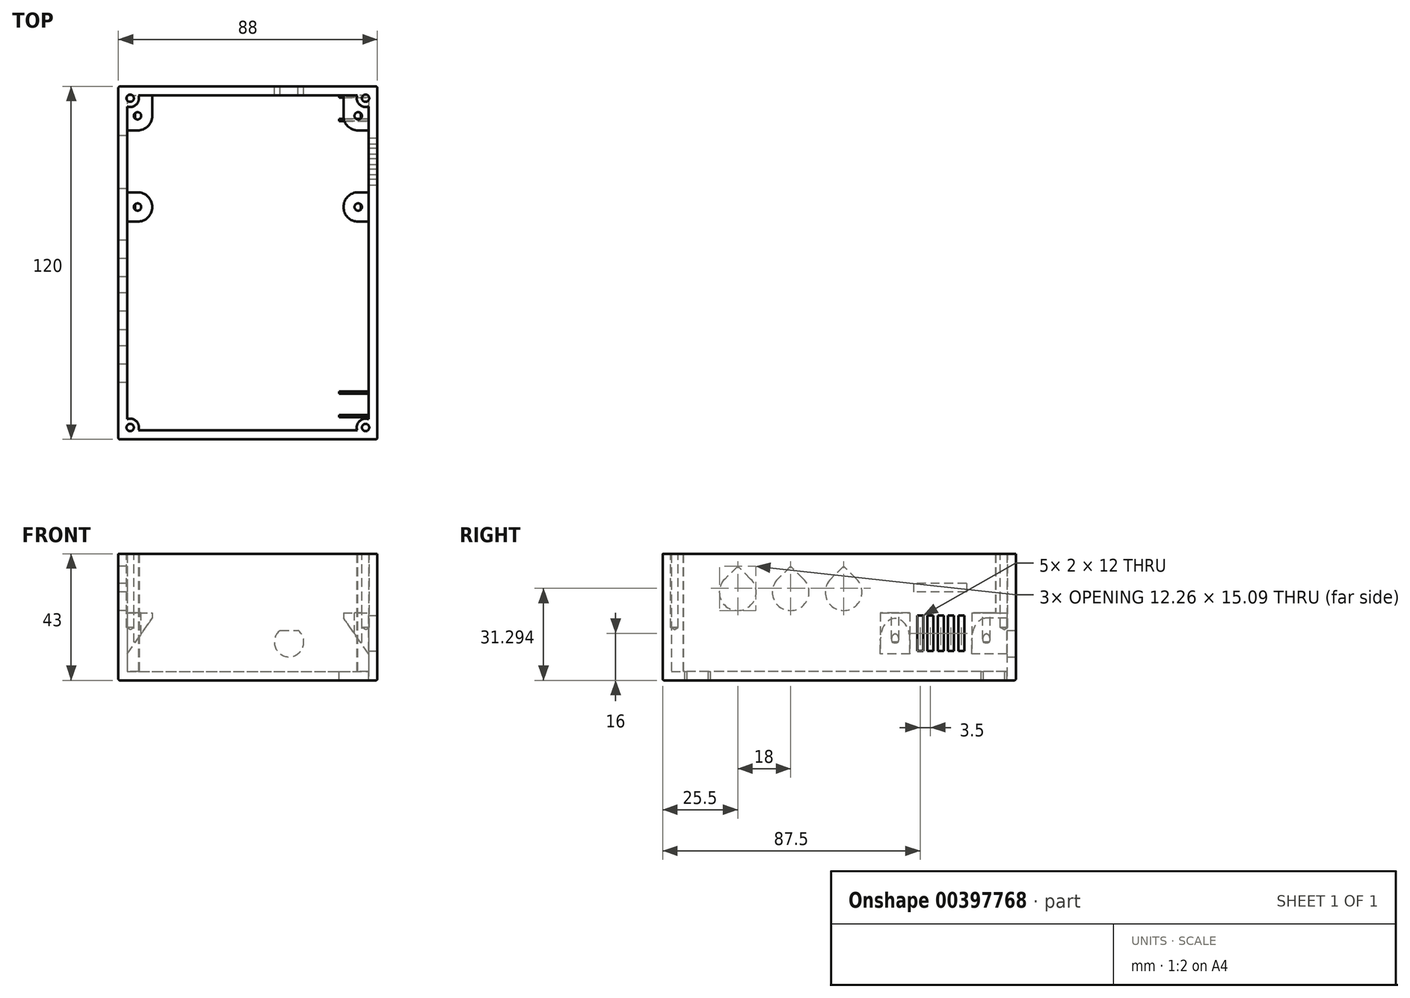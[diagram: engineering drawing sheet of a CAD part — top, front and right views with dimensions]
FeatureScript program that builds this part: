
annotation { "Feature Type Name" : "Feature", "Feature Type Description" : "" }
export const myFeature = defineFeature(function(context is Context, id is Id, definition is map)
    precondition{}
    {
        {
            var Q0;
            Q0=qCreatedBy(makeId("Top.planeOp"),FACE);
            var sketch = newSketch(context, id + "F0", { "sketchPlane" : qUnion([Q0])});
            skLineSegment(sketch, "E0.bottom", {"start": v(0, 0) * mm, "end": v(88, 0) * mm});
            skLineSegment(sketch, "E0.top", {"start": v(0, 120) * mm, "end": v(88, 120) * mm});
            skLineSegment(sketch, "E0.left", {"start": v(0, 0) * mm, "end": v(0, 120) * mm});
            skLineSegment(sketch, "E0.right", {"start": v(88, 0) * mm, "end": v(88, 120) * mm});
            skSolve(sketch);
        }
        {
            var Q0;
            Q0 = qSketchRegion(id + "F0", true);
            extrude(context, id + "F1", {"entities" : qUnion([Q0]), "depth" : 3 * mm});
        }
        {
            var Q0;
            Q0=makeQuery(id+"F1.opExtrude","CAP_FACE",FACE,{"disambiguationData":[OSD([sQuery(id+"F0.wireOp",EDGE,"E0.bottom"),sQuery(id+"F0.wireOp",EDGE,"E0.top"),sQuery(id+"F0.wireOp",EDGE,"E0.left"),sQuery(id+"F0.wireOp",EDGE,"E0.right")])],"isStart":false});
            var sketch = newSketch(context, id + "F2", { "sketchPlane" : qUnion([Q0])});
            skLineSegment(sketch, "E1.0", {"start": v(0, 0) * mm, "end": v(0, 120) * mm});
            skLineSegment(sketch, "E2.0", {"start": v(0, 120) * mm, "end": v(88, 120) * mm});
            skLineSegment(sketch, "E3.0", {"start": v(88, 0) * mm, "end": v(88, 120) * mm});
            skLineSegment(sketch, "E4.0", {"start": v(0, 0) * mm, "end": v(88, 0) * mm});
            skLineSegment(sketch, "E5.bottom", {"start": v(6.83, 117) * mm, "end": v(81.17, 117) * mm});
            skLineSegment(sketch, "E5.top", {"start": v(6.83, 3) * mm, "end": v(81.17, 3) * mm});
            skLineSegment(sketch, "E5.left", {"start": v(3, 113.17) * mm, "end": v(3, 6.83) * mm});
            skLineSegment(sketch, "E5.right", {"start": v(85, 113.17) * mm, "end": v(85, 6.83) * mm});
            skArc(sketch, "E6", {"start": v(3, 113.17) * mm, "mid": v(6.12, 113.88) * mm, "end": v(6.83, 117) * mm});
            skArc(sketch, "E7", {"start": v(81.17, 117) * mm, "mid": v(81.88, 113.88) * mm, "end": v(85, 113.17) * mm});
            skArc(sketch, "E8", {"start": v(6.83, 3) * mm, "mid": v(6.12, 6.12) * mm, "end": v(3, 6.83) * mm});
            skArc(sketch, "E9", {"start": v(85, 6.83) * mm, "mid": v(81.88, 6.12) * mm, "end": v(81.17, 3) * mm});
            skSolve(sketch);
        }
        {
            var Q0;
            Q0 = qSketchRegion(id + "F2", true);
            extrude(context, id + "F3", {"entities" : qUnion([Q0]), "operationType" : NewBodyOperationType.ADD, "depth" : 40 * mm});
        }
        {
            var Q0;
            Q0=makeQuery(id+"F3.boolean.opBoolean","MERGE",FACE,{"derivedFrom":[makeQuery(id+"F1.opExtrude","SWEPT_FACE",FACE,{"disambiguationData":[OSD([sQuery(id+"F0.wireOp",EDGE,"E0.left")])]}),makeQuery(id+"F3.opExtrude","SWEPT_FACE",FACE,{"disambiguationData":[OSD([sQuery(id+"F2.wireOp",EDGE,"E1.0")])]})]});
            var sketch = newSketch(context, id + "F4", { "sketchPlane" : qUnion([Q0])});
            skArc(sketch, "E10", {"start": v(-65.92, 34.42) * mm, "mid": v(-61.5, 23.75) * mm, "end": v(-57.08, 34.42) * mm});
            skLineSegment(sketch, "E11", {"start": v(-65.92, 34.42) * mm, "end": v(-61.5, 38.84) * mm});
            skLineSegment(sketch, "E12", {"start": v(-61.5, 38.84) * mm, "end": v(-57.08, 34.42) * mm});
            skLineSegment(sketch, "E13.1.0.0", {"start": v(-43.5, 38.84) * mm, "end": v(-39.08, 34.42) * mm});
            skLineSegment(sketch, "E13.1.0.1", {"start": v(-47.92, 34.42) * mm, "end": v(-43.5, 38.84) * mm});
            skArc(sketch, "E13.1.0.2", {"start": v(-47.92, 34.42) * mm, "mid": v(-43.5, 23.75) * mm, "end": v(-39.08, 34.42) * mm});
            skLineSegment(sketch, "E13.2.0.0", {"start": v(-25.5, 38.84) * mm, "end": v(-21.08, 34.42) * mm});
            skLineSegment(sketch, "E13.2.0.1", {"start": v(-29.92, 34.42) * mm, "end": v(-25.5, 38.84) * mm});
            skArc(sketch, "E13.2.0.2", {"start": v(-29.92, 34.42) * mm, "mid": v(-25.5, 23.75) * mm, "end": v(-21.08, 34.42) * mm});
            skLineSegment(sketch, "E13.direction1", {"start": v(-61.5, 30) * mm, "end": v(-43.5, 30) * mm, "construction": true});
            skSolve(sketch);
        }
        {
            var Q0;
            Q0 = qSketchRegion(id + "F4", true);
            extrude(context, id + "F5", {"entities" : qUnion([Q0]), "operationType" : NewBodyOperationType.REMOVE, "endBound" : BoundingType.UP_TO_NEXT, "oppositeDirection" : true, "depth" : 25 * mm});
        }
        {
            var Q0;
            Q0=makeQuery(id+"F3.boolean.opBoolean","MERGE",FACE,{"derivedFrom":[makeQuery(id+"F1.opExtrude","SWEPT_FACE",FACE,{"disambiguationData":[OSD([sQuery(id+"F0.wireOp",EDGE,"E0.top")])]}),makeQuery(id+"F3.opExtrude","SWEPT_FACE",FACE,{"disambiguationData":[OSD([sQuery(id+"F2.wireOp",EDGE,"E2.0")])]})]});
            var sketch = newSketch(context, id + "F6", { "sketchPlane" : qUnion([Q0])});
            skArc(sketch, "E14", {"start": v(-61.07, 16.95) * mm, "mid": v(-58, 8) * mm, "end": v(-54.93, 16.95) * mm});
            skLineSegment(sketch, "E15", {"start": v(-61.07, 16.95) * mm, "end": v(-54.93, 16.95) * mm});
            skSolve(sketch);
        }
        {
            var Q0;
            Q0 = qSketchRegion(id + "F6", true);
            extrude(context, id + "F7", {"entities" : qUnion([Q0]), "operationType" : NewBodyOperationType.REMOVE, "endBound" : BoundingType.UP_TO_NEXT, "oppositeDirection" : true, "depth" : 25 * mm});
        }
        {
            var Q0;
            Q0=makeQuery(id+"F1.opExtrude","CAP_EDGE",EDGE,{"disambiguationData":[OSD([sQuery(id+"F0.wireOp",EDGE,"E0.left")])],"isStart":true});
            var Q1;
            Q1=makeQuery(id+"F1.opExtrude","CAP_EDGE",EDGE,{"disambiguationData":[OSD([sQuery(id+"F0.wireOp",EDGE,"E0.bottom")])],"isStart":true});
            var Q2;
            Q2=makeQuery(id+"F3.boolean.opBoolean","MERGE",EDGE,{"derivedFrom":[makeQuery(id+"F1.opExtrude","SWEPT_EDGE",EDGE,{"disambiguationData":[OSD([sQuery(id+"F0.wireOp",EDGE,"E0.bottom"),sQuery(id+"F0.wireOp",EDGE,"E0.left")])]}),makeQuery(id+"F3.opExtrude","SWEPT_EDGE",EDGE,{"disambiguationData":[OSD([sQuery(id+"F2.wireOp",EDGE,"E1.0"),sQuery(id+"F2.wireOp",EDGE,"E4.0")])]})]});
            var Q3;
            Q3=makeQuery(id+"F3.boolean.opBoolean","MERGE",EDGE,{"derivedFrom":[makeQuery(id+"F1.opExtrude","SWEPT_EDGE",EDGE,{"disambiguationData":[OSD([sQuery(id+"F0.wireOp",EDGE,"E0.top"),sQuery(id+"F0.wireOp",EDGE,"E0.left")])]}),makeQuery(id+"F3.opExtrude","SWEPT_EDGE",EDGE,{"disambiguationData":[OSD([sQuery(id+"F2.wireOp",EDGE,"E1.0"),sQuery(id+"F2.wireOp",EDGE,"E2.0")])]})]});
            var Q4;
            Q4=makeQuery(id+"F3.boolean.opBoolean","MERGE",EDGE,{"derivedFrom":[makeQuery(id+"F1.opExtrude","SWEPT_EDGE",EDGE,{"disambiguationData":[OSD([sQuery(id+"F0.wireOp",EDGE,"E0.bottom"),sQuery(id+"F0.wireOp",EDGE,"E0.right")])]}),makeQuery(id+"F3.opExtrude","SWEPT_EDGE",EDGE,{"disambiguationData":[OSD([sQuery(id+"F2.wireOp",EDGE,"E3.0"),sQuery(id+"F2.wireOp",EDGE,"E4.0")])]})]});
            var Q5;
            Q5=makeQuery(id+"F1.opExtrude","CAP_EDGE",EDGE,{"disambiguationData":[OSD([sQuery(id+"F0.wireOp",EDGE,"E0.right")])],"isStart":true});
            var Q6;
            Q6=makeQuery(id+"F1.opExtrude","CAP_EDGE",EDGE,{"disambiguationData":[OSD([sQuery(id+"F0.wireOp",EDGE,"E0.top")])],"isStart":true});
            var Q7;
            Q7=makeQuery(id+"F3.boolean.opBoolean","MERGE",EDGE,{"derivedFrom":[makeQuery(id+"F1.opExtrude","SWEPT_EDGE",EDGE,{"disambiguationData":[OSD([sQuery(id+"F0.wireOp",EDGE,"E0.top"),sQuery(id+"F0.wireOp",EDGE,"E0.right")])]}),makeQuery(id+"F3.opExtrude","SWEPT_EDGE",EDGE,{"disambiguationData":[OSD([sQuery(id+"F2.wireOp",EDGE,"E2.0"),sQuery(id+"F2.wireOp",EDGE,"E3.0")])]})]});
            fillet(context, id + "F8", {"entities" : qUnion([Q0, Q1, Q2, Q3, Q4, Q5, Q6, Q7]), "radius" : 0.5 * mm, "tangentPropagation" : true, "allowEdgeOverflow" : false});
        }
        {
            var Q0;
            Q0=makeQuery(id+"F1.opExtrude","CAP_FACE",FACE,{"disambiguationData":[OSD([sQuery(id+"F0.wireOp",EDGE,"E0.bottom"),sQuery(id+"F0.wireOp",EDGE,"E0.top"),sQuery(id+"F0.wireOp",EDGE,"E0.left"),sQuery(id+"F0.wireOp",EDGE,"E0.right")])],"isStart":false});
            var sketch = newSketch(context, id + "F9", { "sketchPlane" : qUnion([Q0])});
            skLineSegment(sketch, "E16.bottom", {"start": v(6.5, 110) * mm, "end": v(81.5, 110) * mm, "construction": true});
            skLineSegment(sketch, "E16.top", {"start": v(6.5, 79) * mm, "end": v(81.5, 79) * mm, "construction": true});
            skLineSegment(sketch, "E16.left", {"start": v(6.5, 110) * mm, "end": v(6.5, 79) * mm, "construction": true});
            skLineSegment(sketch, "E16.right", {"start": v(81.5, 110) * mm, "end": v(81.5, 79) * mm, "construction": true});
            skArc(sketch, "E17", {"start": v(6.5, 105) * mm, "mid": v(10.04, 106.46) * mm, "end": v(11.5, 110) * mm});
            skArc(sketch, "E18", {"start": v(76.5, 110) * mm, "mid": v(77.96, 106.46) * mm, "end": v(81.5, 105) * mm});
            skArc(sketch, "E19", {"start": v(6.5, 74) * mm, "mid": v(11.5, 79) * mm, "end": v(6.5, 84) * mm});
            skArc(sketch, "E20", {"start": v(81.5, 84) * mm, "mid": v(76.5, 79) * mm, "end": v(81.5, 74) * mm});
            skPoint(sketch, "E21", {"position": v(44, 110) * mm});
            skLineSegment(sketch, "E22", {"start": v(11.5, 110) * mm, "end": v(11.5, 117) * mm});
            skLineSegment(sketch, "E23", {"start": v(6.5, 105) * mm, "end": v(3, 105) * mm});
            skLineSegment(sketch, "E24", {"start": v(6.5, 84) * mm, "end": v(3, 84) * mm});
            skLineSegment(sketch, "E25", {"start": v(6.5, 74) * mm, "end": v(3, 74) * mm});
            skLineSegment(sketch, "E26", {"start": v(81.5, 84) * mm, "end": v(85, 84) * mm});
            skLineSegment(sketch, "E27", {"start": v(76.5, 110) * mm, "end": v(76.5, 117) * mm});
            skLineSegment(sketch, "E28", {"start": v(81.5, 105) * mm, "end": v(85, 105) * mm});
            skLineSegment(sketch, "E29", {"start": v(81.5, 74) * mm, "end": v(85, 74) * mm});
            skSolve(sketch);
        }
        {
            var Q0;
            Q0=makeQuery(id+"F9.imprint","IMPRINT",FACE,{"disambiguationData":[TD([[makeQuery(id+"F9.imprint","IMPRINT",EDGE,{"derivedFrom":sQuery(id+"F9.wireOp",EDGE,"E19")}),1.0]])]});
            var Q1;
            Q1=makeQuery(id+"F9.imprint","IMPRINT",FACE,{"disambiguationData":[TD([[makeQuery(id+"F9.imprint","IMPRINT",EDGE,{"derivedFrom":sQuery(id+"F9.wireOp",EDGE,"E17")}),1.0]])]});
            var Q2;
            Q2=makeQuery(id+"F9.imprint","IMPRINT",FACE,{"disambiguationData":[TD([[makeQuery(id+"F9.imprint","IMPRINT",EDGE,{"derivedFrom":sQuery(id+"F9.wireOp",EDGE,"E18")}),1.0]])]});
            var Q3;
            Q3=makeQuery(id+"F9.imprint","IMPRINT",FACE,{"disambiguationData":[TD([[makeQuery(id+"F9.imprint","IMPRINT",EDGE,{"derivedFrom":sQuery(id+"F9.wireOp",EDGE,"E20")}),1.0]])]});
            var Q4;
            Q4 = qBodyType(qCreatedBy(id + "F11" ,FACE), BodyType.SOLID);
            extrude(context, id + "F10", {"entities" : qUnion([Q0, Q1, Q2, Q3]), "operationType" : NewBodyOperationType.ADD, "endBoundEntityFace" : qUnion([Q4]), "depth" : 20 * mm});
        }
        {
            var Q0;
            Q0=makeQuery(id+"F3.opExtrude","CAP_FACE",FACE,{"disambiguationData":[OSD([sQuery(id+"F2.wireOp",EDGE,"E1.0"),sQuery(id+"F2.wireOp",EDGE,"E2.0"),sQuery(id+"F2.wireOp",EDGE,"E3.0"),sQuery(id+"F2.wireOp",EDGE,"E4.0"),sQuery(id+"F2.wireOp",EDGE,"E5.bottom"),sQuery(id+"F2.wireOp",EDGE,"E5.top"),sQuery(id+"F2.wireOp",EDGE,"E5.left"),sQuery(id+"F2.wireOp",EDGE,"E5.right"),sQuery(id+"F2.wireOp",EDGE,"RnDwJznH-ddYd-c09x-nSyI-hqBMwT2M9eLy"),sQuery(id+"F2.wireOp",EDGE,"lanDXxh8-xAsg-iwlZ-IwJ3-5rcP5cadt3KI"),sQuery(id+"F2.wireOp",EDGE,"uzteUbjJ-Ywx2-gnPR-lJzB-qWgk53przGQ1"),sQuery(id+"F2.wireOp",EDGE,"n90Oo4IX-6F6r-3Tcr-m6S5-17WScgTX6qWq")])],"isStart":false});
            cPlane(context, id + "F11", {"entities" : qUnion([Q0]), "cplaneType" : CPlaneType.OFFSET, "offset" : 20 * mm, "oppositeDirection" : true, "width" : 150 * mm, "height" : 150 * mm});
        }
        {
            var Q0;
            Q0=qCreatedBy(id+"F11.planeOp",FACE);
            var sketch = newSketch(context, id + "F12", { "sketchPlane" : qUnion([Q0])});
            skArc(sketch, "E30.0", {"start": v(6.5, 105) * mm, "mid": v(10.04, 106.46) * mm, "end": v(11.5, 110) * mm, "construction": true});
            skArc(sketch, "E31.0", {"start": v(6.5, 74) * mm, "mid": v(11.5, 79) * mm, "end": v(6.5, 84) * mm, "construction": true});
            skArc(sketch, "E32.0", {"start": v(81.5, 84) * mm, "mid": v(76.5, 79) * mm, "end": v(81.5, 74) * mm, "construction": true});
            skArc(sketch, "E33.0", {"start": v(76.5, 110) * mm, "mid": v(77.96, 106.46) * mm, "end": v(81.5, 105) * mm, "construction": true});
            skSolve(sketch);
        }
        {
            var Q0;
            Q0=sQuery(id+"F12.wireOp",VERTEX,"E30.0.center");
            var Q1;
            Q1=sQuery(id+"F12.wireOp",VERTEX,"E31.0.center");
            var Q2;
            Q2=sQuery(id+"F12.wireOp",VERTEX,"E32.0.center");
            var Q3;
            Q3=sQuery(id+"F12.wireOp",VERTEX,"E33.0.center");
            var Q4;
            Q4=makeQuery(id+"F1.opExtrude","SWEPT_BODY",BODY,{"disambiguationData":[OSD([sQuery(id+"F0.wireOp",EDGE,"E0.bottom"),sQuery(id+"F0.wireOp",EDGE,"E0.top"),sQuery(id+"F0.wireOp",EDGE,"E0.left"),sQuery(id+"F0.wireOp",EDGE,"E0.right")])]});
            hole(context, id + "F13", {"style" : HoleStyle.SIMPLE, "endStyle" : HoleEndStyle.BLIND, "holeDiameter" : 2.5 * mm, "holeDepth" : 10 * mm, "isTappedThrough" : true, "tappedDepth" : 12 * mm, "tapClearance" : 3, "locations" : qUnion([Q0, Q1, Q2, Q3]), "scope" : qUnion([Q4])});
        }
        {
            var Q0;
            Q0=makeQuery(id+"F10.opExtrude","SWEPT_FACE",FACE,{"disambiguationData":[OSD([sQuery(id+"F9.wireOp",EDGE,"E29")])]});
            var sketch = newSketch(context, id + "F14", { "sketchPlane" : qUnion([Q0])});
            skLineSegment(sketch, "E34", {"start": v(85, 3) * mm, "end": v(85, 9) * mm});
            skLineSegment(sketch, "E35", {"start": v(85, 9) * mm, "end": v(76.5, 21.14) * mm});
            skLineSegment(sketch, "E36", {"start": v(76.5, 21.14) * mm, "end": v(76.5, 3) * mm});
            skLineSegment(sketch, "E37", {"start": v(76.5, 3) * mm, "end": v(85, 3) * mm});
            skSolve(sketch);
        }
        {
            var Q0;
            Q0 = qSketchRegion(id + "F14", true);
            var Q1;
            Q1=makeQuery(id+"F3.opExtrude","SWEPT_FACE",FACE,{"disambiguationData":[OSD([sQuery(id+"F2.wireOp",EDGE,"E5.bottom")])]});
            extrude(context, id + "F15", {"entities" : qUnion([Q0]), "operationType" : NewBodyOperationType.REMOVE, "endBound" : BoundingType.UP_TO_SURFACE, "oppositeDirection" : true, "endBoundEntityFace" : qUnion([Q1]), "depth" : 25 * mm});
        }
        {
            var Q0;
            Q0=makeQuery(id+"F10.opExtrude","SWEPT_FACE",FACE,{"disambiguationData":[OSD([sQuery(id+"F9.wireOp",EDGE,"E25")])]});
            var sketch = newSketch(context, id + "F16", { "sketchPlane" : qUnion([Q0])});
            skLineSegment(sketch, "E38", {"start": v(3, 3) * mm, "end": v(3, 9) * mm});
            skLineSegment(sketch, "E39", {"start": v(3, 9) * mm, "end": v(11.5, 21.14) * mm});
            skLineSegment(sketch, "E40", {"start": v(11.5, 21.14) * mm, "end": v(11.5, 3) * mm});
            skLineSegment(sketch, "E41", {"start": v(11.5, 3) * mm, "end": v(3, 3) * mm});
            skSolve(sketch);
        }
        {
            var Q0;
            Q0 = qSketchRegion(id + "F16", true);
            var Q1;
            {var subQ0=sQuery(id+"F2.wireOp",EDGE,"E5.bottom");Q1=makeQuery(id+"F15.boolean.opBoolean","MERGE",FACE,{"derivedFrom":[makeQuery(id+"F3.opExtrude","SWEPT_FACE",FACE,{"disambiguationData":[OSD([subQ0])]}),makeQuery(id+"F15.opExtrude","CAP_FACE",FACE,{"disambiguationData":[OSD([subQ0])],"isStart":false})]});}
            extrude(context, id + "F17", {"entities" : qUnion([Q0]), "operationType" : NewBodyOperationType.REMOVE, "endBound" : BoundingType.UP_TO_SURFACE, "oppositeDirection" : true, "endBoundEntityFace" : qUnion([Q1]), "depth" : 25 * mm});
        }
        {
            var Q0;
            Q0=makeQuery(id+"F17.boolean.opBoolean","MERGE",FACE,{"derivedFrom":[makeQuery(id+"F15.boolean.opBoolean","MERGE",FACE,{"derivedFrom":[makeQuery(id+"F1.opExtrude","CAP_FACE",FACE,{"disambiguationData":[OSD([sQuery(id+"F0.wireOp",EDGE,"E0.bottom"),sQuery(id+"F0.wireOp",EDGE,"E0.top"),sQuery(id+"F0.wireOp",EDGE,"E0.left"),sQuery(id+"F0.wireOp",EDGE,"E0.right")])],"isStart":false}),makeQuery(id+"F15.opExtrude","SWEPT_FACE",FACE,{"disambiguationData":[OSD([sQuery(id+"F14.wireOp",EDGE,"E37")])]})]}),makeQuery(id+"F17.opExtrude","SWEPT_FACE",FACE,{"disambiguationData":[OSD([sQuery(id+"F16.wireOp",EDGE,"E41")])]})]});
            var sketch = newSketch(context, id + "F18", { "sketchPlane" : qUnion([Q0])});
            skLineSegment(sketch, "E42.bottom", {"start": v(75, 8.25) * mm, "end": v(85, 8.25) * mm});
            skLineSegment(sketch, "E42.top", {"start": v(75, 7.5) * mm, "end": v(85, 7.5) * mm});
            skLineSegment(sketch, "E42.left", {"start": v(75, 7.5) * mm, "end": v(75, 8.25) * mm});
            skLineSegment(sketch, "E42.right", {"start": v(85, 7.5) * mm, "end": v(85, 8.25) * mm});
            skLineSegment(sketch, "E43.bottom", {"start": v(75, 15.5) * mm, "end": v(85, 15.5) * mm});
            skLineSegment(sketch, "E43.top", {"start": v(75, 16.25) * mm, "end": v(85, 16.25) * mm});
            skLineSegment(sketch, "E43.left", {"start": v(75, 15.5) * mm, "end": v(75, 16.25) * mm});
            skLineSegment(sketch, "E43.right", {"start": v(85, 15.5) * mm, "end": v(85, 16.25) * mm});
            skLineSegment(sketch, "E44.bottom", {"start": v(75, 108.25) * mm, "end": v(85, 108.25) * mm});
            skLineSegment(sketch, "E44.top", {"start": v(75, 109) * mm, "end": v(85, 109) * mm});
            skLineSegment(sketch, "E44.left", {"start": v(75, 108.25) * mm, "end": v(75, 109) * mm});
            skLineSegment(sketch, "E44.right", {"start": v(85, 108.25) * mm, "end": v(85, 109) * mm});
            skLineSegment(sketch, "E45.bottom", {"start": v(75, 116.25) * mm, "end": v(85, 116.25) * mm});
            skLineSegment(sketch, "E45.top", {"start": v(75, 117) * mm, "end": v(85, 117) * mm});
            skLineSegment(sketch, "E45.left", {"start": v(75, 116.25) * mm, "end": v(75, 117) * mm});
            skLineSegment(sketch, "E45.right", {"start": v(85, 116.25) * mm, "end": v(85, 117) * mm});
            skSolve(sketch);
        }
        {
            var Q0;
            Q0 = qSketchRegion(id + "F18", true);
            var Q1;
            Q1=makeQuery(id+"F1.opExtrude","CAP_FACE",FACE,{"disambiguationData":[OSD([sQuery(id+"F0.wireOp",EDGE,"E0.bottom"),sQuery(id+"F0.wireOp",EDGE,"E0.top"),sQuery(id+"F0.wireOp",EDGE,"E0.left"),sQuery(id+"F0.wireOp",EDGE,"E0.right")])],"isStart":true});
            extrude(context, id + "F19", {"entities" : qUnion([Q0]), "operationType" : NewBodyOperationType.REMOVE, "endBound" : BoundingType.UP_TO_SURFACE, "oppositeDirection" : true, "endBoundEntityFace" : qUnion([Q1]), "depth" : 25 * mm});
        }
        {
            var Q0;
            Q0=makeQuery(id+"F3.opExtrude","CAP_FACE",FACE,{"disambiguationData":[OSD([sQuery(id+"F2.wireOp",EDGE,"E1.0"),sQuery(id+"F2.wireOp",EDGE,"E2.0"),sQuery(id+"F2.wireOp",EDGE,"E3.0"),sQuery(id+"F2.wireOp",EDGE,"E4.0"),sQuery(id+"F2.wireOp",EDGE,"E5.bottom"),sQuery(id+"F2.wireOp",EDGE,"E5.top"),sQuery(id+"F2.wireOp",EDGE,"E5.left"),sQuery(id+"F2.wireOp",EDGE,"E5.right"),sQuery(id+"F2.wireOp",EDGE,"E6"),sQuery(id+"F2.wireOp",EDGE,"E7"),sQuery(id+"F2.wireOp",EDGE,"E8"),sQuery(id+"F2.wireOp",EDGE,"E9")])],"isStart":false});
            var sketch = newSketch(context, id + "F20", { "sketchPlane" : qUnion([Q0])});
            skLineSegment(sketch, "E46.bottom", {"start": v(4, 116) * mm, "end": v(84, 116) * mm, "construction": true});
            skLineSegment(sketch, "E46.top", {"start": v(4, 4) * mm, "end": v(84, 4) * mm, "construction": true});
            skLineSegment(sketch, "E46.left", {"start": v(4, 116) * mm, "end": v(4, 4) * mm, "construction": true});
            skLineSegment(sketch, "E46.right", {"start": v(84, 116) * mm, "end": v(84, 4) * mm, "construction": true});
            skSolve(sketch);
        }
        {
            var Q0;
            Q0=sQuery(id+"F20.wireOp",VERTEX,"E46.left.start");
            var Q1;
            Q1=sQuery(id+"F20.wireOp",VERTEX,"E46.left.end");
            var Q2;
            Q2=sQuery(id+"F20.wireOp",VERTEX,"E46.right.end");
            var Q3;
            Q3=sQuery(id+"F20.wireOp",VERTEX,"E46.right.start");
            var Q4;
            Q4=makeQuery(id+"F1.opExtrude","SWEPT_BODY",BODY,{"disambiguationData":[OSD([sQuery(id+"F0.wireOp",EDGE,"E0.bottom"),sQuery(id+"F0.wireOp",EDGE,"E0.top"),sQuery(id+"F0.wireOp",EDGE,"E0.left"),sQuery(id+"F0.wireOp",EDGE,"E0.right")])]});
            hole(context, id + "F21", {"style" : HoleStyle.SIMPLE, "endStyle" : HoleEndStyle.BLIND, "holeDiameter" : 2.5 * mm, "holeDepth" : 25 * mm, "isTappedThrough" : true, "tappedDepth" : 12 * mm, "tapClearance" : 3, "locations" : qUnion([Q0, Q1, Q2, Q3]), "scope" : qUnion([Q4])});
        }
        {
            var Q0;
            Q0=makeQuery(id+"F3.boolean.opBoolean","MERGE",FACE,{"derivedFrom":[makeQuery(id+"F1.opExtrude","SWEPT_FACE",FACE,{"disambiguationData":[OSD([sQuery(id+"F0.wireOp",EDGE,"E0.left")])]}),makeQuery(id+"F3.opExtrude","SWEPT_FACE",FACE,{"disambiguationData":[OSD([sQuery(id+"F2.wireOp",EDGE,"E1.0")])]})]});
            var sketch = newSketch(context, id + "F22", { "sketchPlane" : qUnion([Q0])});
            skLineSegment(sketch, "E47.0", {"start": v(-110, 23) * mm, "end": v(-117, 23) * mm, "construction": true});
            skLineSegment(sketch, "E48.bottom", {"start": v(-103.25, 33) * mm, "end": v(-85.25, 33) * mm});
            skLineSegment(sketch, "E48.top", {"start": v(-103.25, 30) * mm, "end": v(-85.25, 30) * mm});
            skLineSegment(sketch, "E48.left", {"start": v(-103.25, 33) * mm, "end": v(-103.25, 30) * mm});
            skLineSegment(sketch, "E48.right", {"start": v(-85.25, 33) * mm, "end": v(-85.25, 30) * mm});
            skLineSegment(sketch, "E49", {"start": v(-111.25, 14) * mm, "end": v(-111.25, 24) * mm, "construction": true});
            skSolve(sketch);
        }
        {
            var Q0;
            Q0=makeQuery(id+"F22.imprint","IMPRINT",FACE,{"disambiguationData":[TD([[makeQuery(id+"F22.imprint","IMPRINT",EDGE,{"derivedFrom":sQuery(id+"F22.wireOp",EDGE,"E48.bottom")}),-1.0]])]});
            var Q1;
            Q1=makeQuery(id+"F17.boolean.opBoolean","MERGE",FACE,{"derivedFrom":[makeQuery(id+"F3.opExtrude","SWEPT_FACE",FACE,{"disambiguationData":[OSD([sQuery(id+"F2.wireOp",EDGE,"E5.left")])]}),makeQuery(id+"F17.opExtrude","SWEPT_FACE",FACE,{"disambiguationData":[OSD([sQuery(id+"F16.wireOp",EDGE,"E38")])]})]});
            extrude(context, id + "F23", {"entities" : qUnion([Q0]), "operationType" : NewBodyOperationType.REMOVE, "endBound" : BoundingType.UP_TO_SURFACE, "oppositeDirection" : true, "endBoundEntityFace" : qUnion([Q1]), "depth" : 25 * mm});
        }
        {
            var Q0;
            Q0=makeQuery(id+"F3.boolean.opBoolean","MERGE",FACE,{"derivedFrom":[makeQuery(id+"F1.opExtrude","SWEPT_FACE",FACE,{"disambiguationData":[OSD([sQuery(id+"F0.wireOp",EDGE,"E0.right")])]}),makeQuery(id+"F3.opExtrude","SWEPT_FACE",FACE,{"disambiguationData":[OSD([sQuery(id+"F2.wireOp",EDGE,"E3.0")])]})]});
            var sketch = newSketch(context, id + "F24", { "sketchPlane" : qUnion([Q0])});
            skLineSegment(sketch, "E50.0", {"start": v(105, 23) * mm, "end": v(105, 9) * mm, "construction": true});
            skLineSegment(sketch, "E51.0", {"start": v(84, 23) * mm, "end": v(84, 9) * mm, "construction": true});
            skLineSegment(sketch, "E52", {"start": v(84, 23) * mm, "end": v(105, 23) * mm, "construction": true});
            skLineSegment(sketch, "E53", {"start": v(105, 9) * mm, "end": v(84, 9) * mm, "construction": true});
            skLineSegment(sketch, "E54.bottom", {"start": v(86.5, 22) * mm, "end": v(88.5, 22) * mm});
            skLineSegment(sketch, "E54.top", {"start": v(86.5, 10) * mm, "end": v(88.5, 10) * mm});
            skLineSegment(sketch, "E54.left", {"start": v(86.5, 22) * mm, "end": v(86.5, 10) * mm});
            skLineSegment(sketch, "E54.right", {"start": v(88.5, 22) * mm, "end": v(88.5, 10) * mm});
            skLineSegment(sketch, "E55.1.0.0", {"start": v(92, 22) * mm, "end": v(92, 10) * mm});
            skLineSegment(sketch, "E55.1.0.1", {"start": v(90, 10) * mm, "end": v(92, 10) * mm});
            skLineSegment(sketch, "E55.1.0.2", {"start": v(90, 22) * mm, "end": v(92, 22) * mm});
            skLineSegment(sketch, "E55.1.0.3", {"start": v(90, 22) * mm, "end": v(90, 10) * mm});
            skLineSegment(sketch, "E55.2.0.0", {"start": v(95.5, 22) * mm, "end": v(95.5, 10) * mm});
            skLineSegment(sketch, "E55.2.0.1", {"start": v(93.5, 10) * mm, "end": v(95.5, 10) * mm});
            skLineSegment(sketch, "E55.2.0.2", {"start": v(93.5, 22) * mm, "end": v(95.5, 22) * mm});
            skLineSegment(sketch, "E55.2.0.3", {"start": v(93.5, 22) * mm, "end": v(93.5, 10) * mm});
            skLineSegment(sketch, "E55.3.0.0", {"start": v(99, 22) * mm, "end": v(99, 10) * mm});
            skLineSegment(sketch, "E55.3.0.1", {"start": v(97, 10) * mm, "end": v(99, 10) * mm});
            skLineSegment(sketch, "E55.3.0.2", {"start": v(97, 22) * mm, "end": v(99, 22) * mm});
            skLineSegment(sketch, "E55.3.0.3", {"start": v(97, 22) * mm, "end": v(97, 10) * mm});
            skLineSegment(sketch, "E55.4.0.0", {"start": v(102.5, 22) * mm, "end": v(102.5, 10) * mm});
            skLineSegment(sketch, "E55.4.0.1", {"start": v(100.5, 10) * mm, "end": v(102.5, 10) * mm});
            skLineSegment(sketch, "E55.4.0.2", {"start": v(100.5, 22) * mm, "end": v(102.5, 22) * mm});
            skLineSegment(sketch, "E55.4.0.3", {"start": v(100.5, 22) * mm, "end": v(100.5, 10) * mm});
            skLineSegment(sketch, "E55.direction1", {"start": v(86.5, 10) * mm, "end": v(90, 10) * mm, "construction": true});
            skSolve(sketch);
        }
        {
            var Q0;
            Q0 = qSketchRegion(id + "F24", true);
            extrude(context, id + "F25", {"entities" : qUnion([Q0]), "operationType" : NewBodyOperationType.REMOVE, "endBound" : BoundingType.UP_TO_NEXT, "oppositeDirection" : true, "depth" : 25 * mm});
        }
    });
